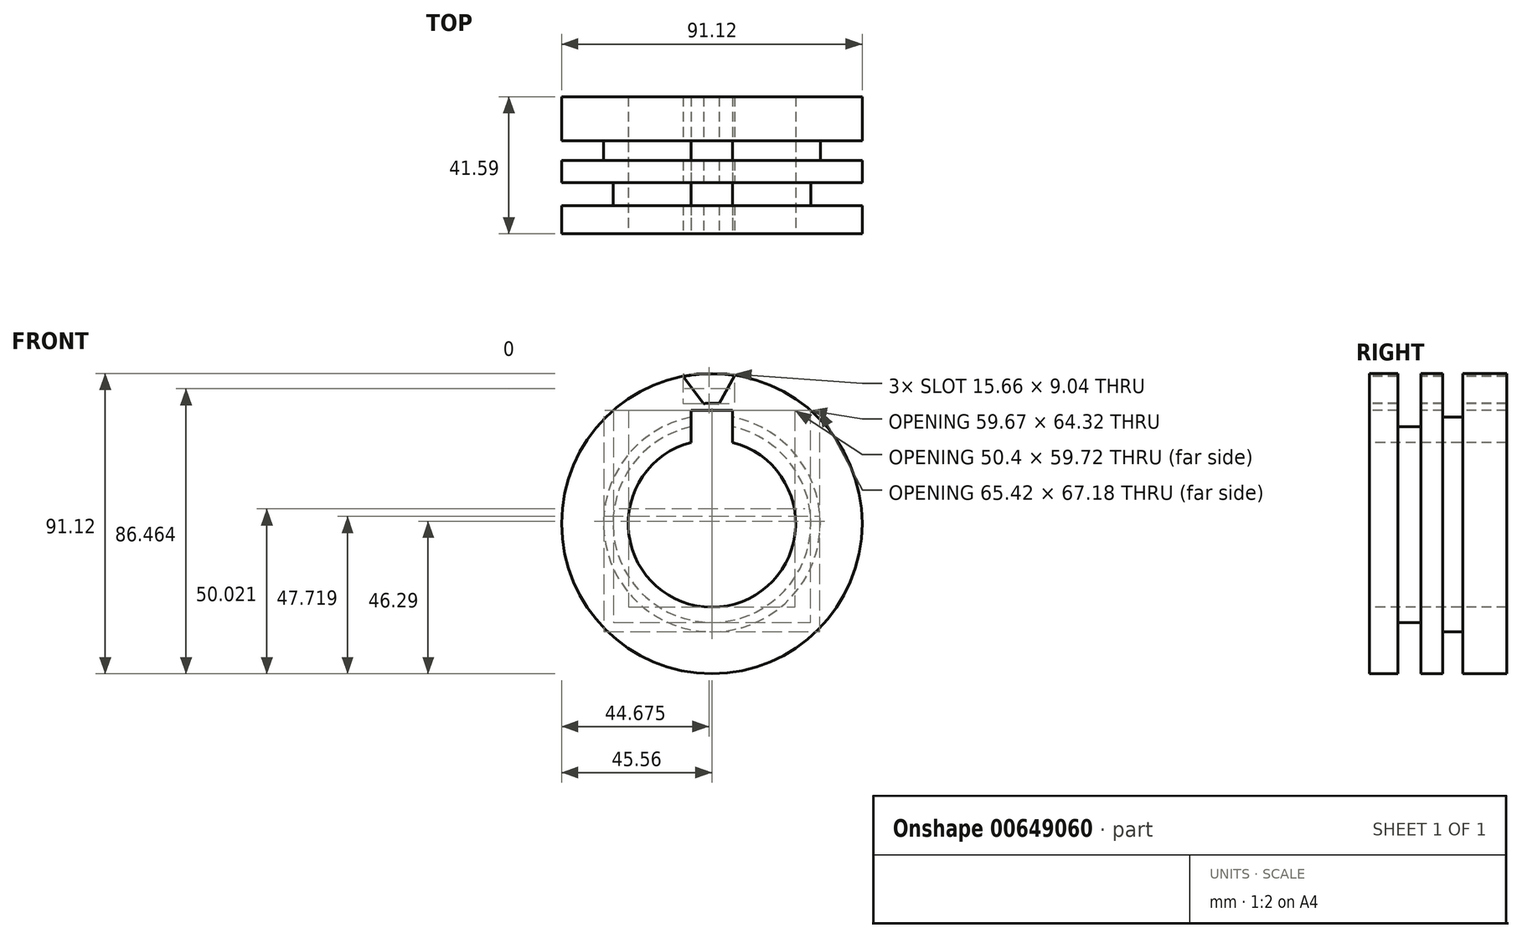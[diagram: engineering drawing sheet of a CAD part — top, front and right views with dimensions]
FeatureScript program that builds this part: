
annotation { "Feature Type Name" : "Feature", "Feature Type Description" : "" }
export const myFeature = defineFeature(function(context is Context, id is Id, definition is map)
    precondition{}
    {
        {
            var Q0;
            Q0=qCreatedBy(makeId("Top.planeOp"),FACE);
            var sketch = newSketch(context, id + "F0", { "sketchPlane" : qUnion([Q0])});
            skLineSegment(sketch, "E0.bottom", {"start": v(0, 0) * mm, "end": v(-45.56, 0) * mm});
            skLineSegment(sketch, "E0.top", {"start": v(0, 41.6) * mm, "end": v(-45.56, 41.6) * mm});
            skLineSegment(sketch, "E0.left", {"start": v(0, 0) * mm, "end": v(0, 41.6) * mm});
            skLineSegment(sketch, "E0.right", {"start": v(-45.56, 0) * mm, "end": v(-45.56, 41.6) * mm});
            skLineSegment(sketch, "E1.bottom", {"start": v(-45.56, 28.26) * mm, "end": v(-32.86, 28.26) * mm});
            skLineSegment(sketch, "E1.top", {"start": v(-45.56, 22.23) * mm, "end": v(-32.86, 22.23) * mm});
            skLineSegment(sketch, "E1.left", {"start": v(-45.56, 28.26) * mm, "end": v(-45.56, 22.23) * mm});
            skLineSegment(sketch, "E1.right", {"start": v(-32.86, 28.26) * mm, "end": v(-32.86, 22.23) * mm});
            skLineSegment(sketch, "E2.bottom", {"start": v(-45.56, 15.56) * mm, "end": v(-30, 15.56) * mm});
            skLineSegment(sketch, "E2.top", {"start": v(-45.56, 8.57) * mm, "end": v(-30, 8.57) * mm});
            skLineSegment(sketch, "E2.left", {"start": v(-45.56, 15.56) * mm, "end": v(-45.56, 8.57) * mm});
            skLineSegment(sketch, "E2.right", {"start": v(-30, 15.56) * mm, "end": v(-30, 8.57) * mm});
            skSolve(sketch);
        }
        {
            var Q0;
            {var subQ7=sQuery(id+"F0.wireOp",EDGE,"E0.bottom");Q0=makeQuery(id+"F0.imprint","IMPRINT",FACE,{"disambiguationData":[TD([[makeQuery(id+"F0.imprint","IMPRINT",EDGE,{"derivedFrom":subQ7}),-1.0]])]});}
            var Q1;
            Q1=sQuery(id+"F0.wireOp",EDGE,"E0.left");
            revolve(context, id + "F1", {"entities" : qUnion([Q0]), "axis" : qUnion([Q1]), "revolveType" : RevolveType.FULL});
        }
        {
            var Q0;
            Q0=makeQuery(id+"F1.opRevolve","SWEPT_FACE",FACE,{"disambiguationData":[OSD([sQuery(id+"F0.wireOp",EDGE,"E0.bottom")])]});
            var sketch = newSketch(context, id + "F2", { "sketchPlane" : qUnion([Q0])});
            skPoint(sketch, "E3", {"position": v(0, 0) * mm});
            skCircle(sketch, "E4", {"center": v(0, 0) * mm, "radius": 25.4 * mm});
            skLineSegment(sketch, "E5.bottom", {"start": v(0, 0) * mm, "end": v(9.63, 0) * mm});
            skLineSegment(sketch, "E5.top", {"start": v(0, 14.1) * mm, "end": v(9.63, 14.1) * mm});
            skLineSegment(sketch, "E5.left", {"start": v(0, 0) * mm, "end": v(0, 14.1) * mm});
            skLineSegment(sketch, "E5.right", {"start": v(9.63, 0) * mm, "end": v(9.63, 14.1) * mm});
            skLineSegment(sketch, "E6.bottom", {"start": v(6.3, 34.32) * mm, "end": v(-6.3, 34.32) * mm});
            skLineSegment(sketch, "E6.top", {"start": v(6.3, -34.32) * mm, "end": v(-6.3, -34.32) * mm});
            skLineSegment(sketch, "E6.left", {"start": v(6.3, 34.32) * mm, "end": v(6.3, -34.32) * mm});
            skLineSegment(sketch, "E6.right", {"start": v(-6.3, 34.32) * mm, "end": v(-6.3, -34.32) * mm});
            skSolve(sketch);
        }
        {
            var Q0;
            Q0=sQuery(id+"F2.wireOp",VERTEX,"E3");
            var Q1;
            Q1=makeQuery(id+"F1.opRevolve","SWEPT_BODY",BODY,{"disambiguationData":[OSD([sQuery(id+"F0.wireOp",EDGE,"E0.bottom"),sQuery(id+"F0.wireOp",EDGE,"E0.top"),sQuery(id+"F0.wireOp",EDGE,"E0.left"),sQuery(id+"F0.wireOp",EDGE,"E0.right"),sQuery(id+"F0.wireOp",EDGE,"E1.bottom"),sQuery(id+"F0.wireOp",EDGE,"E1.top"),sQuery(id+"F0.wireOp",EDGE,"E1.right"),sQuery(id+"F0.wireOp",EDGE,"E2.bottom"),sQuery(id+"F0.wireOp",EDGE,"E2.top"),sQuery(id+"F0.wireOp",EDGE,"E2.right")])]});
            hole(context, id + "F3", {"style" : HoleStyle.SIMPLE, "endStyle" : HoleEndStyle.THROUGH, "standardTappedOrClearance" : lookupTablePath({ "standard" : "ANSI", "fit" : "Close", "size" : "1/2", "type" : "Clearance" }), "standardBlindInLast" : lookupTablePath({ "fit" : "Close", "standard" : "ANSI", "size" : "1/2", "type" : "Clearance" }), "holeDiameter" : 13.1 * mm, "majorDiameter" : 6.35 * mm, "isTappedThrough" : true, "tappedDepth" : 12.7 * mm, "tapClearance" : 3, "startFromSketch" : true, "locations" : qUnion([Q0]), "scope" : qUnion([Q1])});
        }
        {
            var Q0;
            {var subQ5=sQuery(id+"F2.wireOp",EDGE,"E6.bottom");Q0=makeQuery(id+"F2.imprint","IMPRINT",FACE,{"disambiguationData":[TD([[makeQuery(id+"F2.imprint","IMPRINT",EDGE,{"derivedFrom":subQ5}),1.0]])]});}
            var Q1;
            {var subQ0=sQuery(id+"F2.wireOp",EDGE,"E6.right");var subQ1=sQuery(id+"F2.wireOp",EDGE,"E4");var subQ2=makeQuery(id+"F2.imprint","INTERSECT",VERTEX,{"disambiguationData":[OD(0.0)],"derivedFrom":[subQ1,subQ0]});Q1=makeQuery(id+"F2.imprint","IMPRINT",FACE,{"disambiguationData":[TD([[makeQuery(id+"F2.imprint","IMPRINT",EDGE,{"disambiguationData":[TD([[subQ2,-1.0]])],"derivedFrom":subQ1}),1.0]])]});}
            var Q2;
            {var subQ0=sQuery(id+"F2.wireOp",EDGE,"E5.right");Q2=makeQuery(id+"F2.imprint","IMPRINT",FACE,{"disambiguationData":[TD([[makeQuery(id+"F2.imprint","IMPRINT",EDGE,{"derivedFrom":subQ0}),-1.0]])]});}
            var Q3;
            {var subQ0=sQuery(id+"F2.wireOp",EDGE,"E5.left");Q3=makeQuery(id+"F2.imprint","IMPRINT",FACE,{"disambiguationData":[TD([[makeQuery(id+"F2.imprint","IMPRINT",EDGE,{"derivedFrom":subQ0}),1.0]])]});}
            var Q4;
            {var subQ0=sQuery(id+"F2.wireOp",EDGE,"E5.left");Q4=makeQuery(id+"F2.imprint","IMPRINT",FACE,{"disambiguationData":[TD([[makeQuery(id+"F2.imprint","IMPRINT",EDGE,{"derivedFrom":subQ0}),-1.0]])]});}
            var Q5;
            {var subQ0=sQuery(id+"F2.wireOp",EDGE,"E5.right");Q5=makeQuery(id+"F2.imprint","IMPRINT",FACE,{"disambiguationData":[TD([[makeQuery(id+"F2.imprint","IMPRINT",EDGE,{"derivedFrom":subQ0}),1.0]])]});}
            var Q6;
            Q6=sQuery(id+"F2.wireOp",EDGE,"E4");
            extrude(context, id + "F4", {"entities" : qUnion([Q0, Q1, Q2, Q3, Q4, Q5]), "operationType" : NewBodyOperationType.REMOVE, "surfaceEntities" : qUnion([Q6]), "oppositeDirection" : true, "depth" : 121.4 * mm, "offsetDistance" : 25.4 * mm});
        }
        {
            var Q0;
            Q0=makeQuery(id+"F1.opRevolve","SWEPT_FACE",FACE,{"disambiguationData":[OSD([sQuery(id+"F0.wireOp",EDGE,"E0.bottom")])]});
            var sketch = newSketch(context, id + "F5", { "sketchPlane" : qUnion([Q0])});
            skCircle(sketch, "E7", {"center": v(0, 0) * mm, "radius": 36.47 * mm});
            skCircle(sketch, "E8", {"center": v(0, 0) * mm, "radius": 45.43 * mm});
            skLineSegment(sketch, "E9", {"start": v(-2.51, 36.39) * mm, "end": v(-8.8, 44.7) * mm});
            skLineSegment(sketch, "E10", {"start": v(2.21, 36.4) * mm, "end": v(6.95, 44.9) * mm});
            skSolve(sketch);
        }
        {
            var Q0;
            {var subQ3=sQuery(id+"F5.wireOp",EDGE,"E10");Q0=makeQuery(id+"F5.imprint","IMPRINT",FACE,{"disambiguationData":[TD([[makeQuery(id+"F5.imprint","IMPRINT",EDGE,{"derivedFrom":subQ3}),1.0]])]});}
            extrude(context, id + "F6", {"entities" : qUnion([Q0]), "operationType" : NewBodyOperationType.REMOVE, "oppositeDirection" : true, "depth" : 62.23 * mm, "offsetDistance" : 25.4 * mm});
        }
    });
